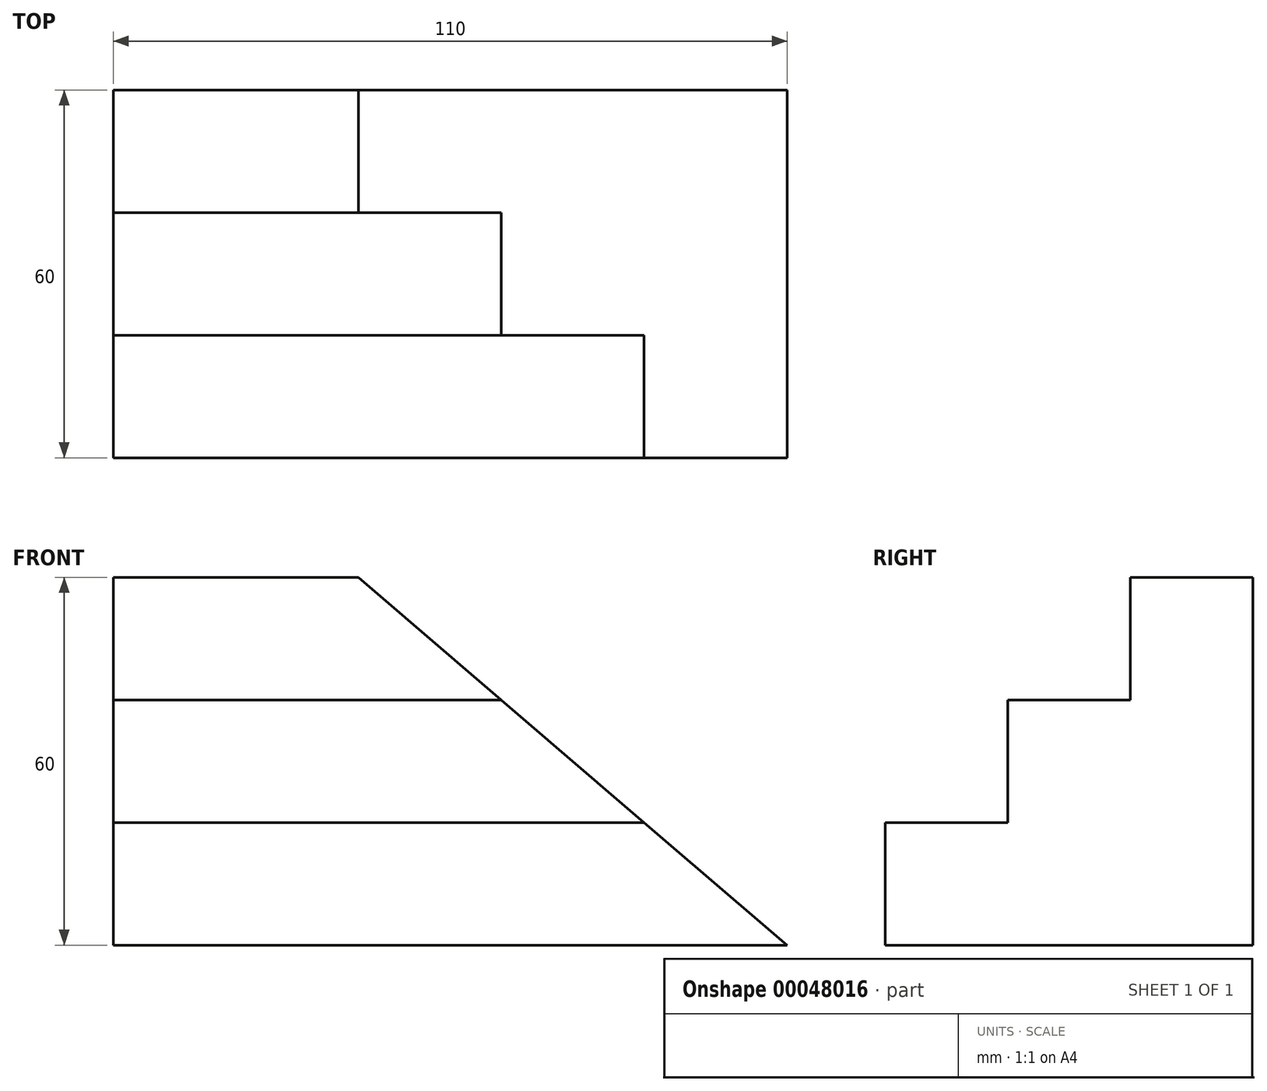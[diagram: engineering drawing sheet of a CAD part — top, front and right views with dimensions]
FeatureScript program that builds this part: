
annotation { "Feature Type Name" : "Feature", "Feature Type Description" : "" }
export const myFeature = defineFeature(function(context is Context, id is Id, definition is map)
    precondition{}
    {
        {
            var Q0;
            Q0=qCreatedBy(makeId("Front.planeOp"),FACE);
            var sketch = newSketch(context, id + "F0", { "sketchPlane" : qUnion([Q0])});
            skLineSegment(sketch, "E0", {"start": v(0, 0) * mm, "end": v(0, 60) * mm});
            skLineSegment(sketch, "E1", {"start": v(0, 60) * mm, "end": v(40, 60) * mm});
            skLineSegment(sketch, "E2", {"start": v(40, 60) * mm, "end": v(110, 0) * mm});
            skLineSegment(sketch, "E3", {"start": v(110, 0) * mm, "end": v(0, 0) * mm});
            skLineSegment(sketch, "E4", {"start": v(0, 20) * mm, "end": v(86.67, 20) * mm});
            skLineSegment(sketch, "E5", {"start": v(0, 40) * mm, "end": v(63.33, 40) * mm});
            skSolve(sketch);
        }
        {
            var Q0;
            {var subQ2=sQuery(id+"F0.wireOp",EDGE,"E1");Q0=makeQuery(id+"F0.imprint","IMPRINT",FACE,{"disambiguationData":[TD([[makeQuery(id+"F0.imprint","IMPRINT",EDGE,{"derivedFrom":subQ2}),-1.0]])]});}
            extrude(context, id + "F1", {"entities" : qUnion([Q0]), "depth" : 20 * mm});
        }
        {
            var Q0;
            {var subQ1=sQuery(id+"F0.wireOp",EDGE,"E4");Q0=makeQuery(id+"F0.imprint","IMPRINT",FACE,{"disambiguationData":[TD([[makeQuery(id+"F0.imprint","IMPRINT",EDGE,{"derivedFrom":subQ1}),1.0]])]});}
            extrude(context, id + "F2", {"entities" : qUnion([Q0]), "operationType" : NewBodyOperationType.ADD, "depth" : 40 * mm});
        }
        {
            var Q0;
            {var subQ1=sQuery(id+"F0.wireOp",EDGE,"E3");Q0=makeQuery(id+"F0.imprint","IMPRINT",FACE,{"disambiguationData":[TD([[makeQuery(id+"F0.imprint","IMPRINT",EDGE,{"derivedFrom":subQ1}),-1.0]])]});}
            extrude(context, id + "F3", {"entities" : qUnion([Q0]), "operationType" : NewBodyOperationType.ADD, "depth" : 60 * mm});
        }
    });
